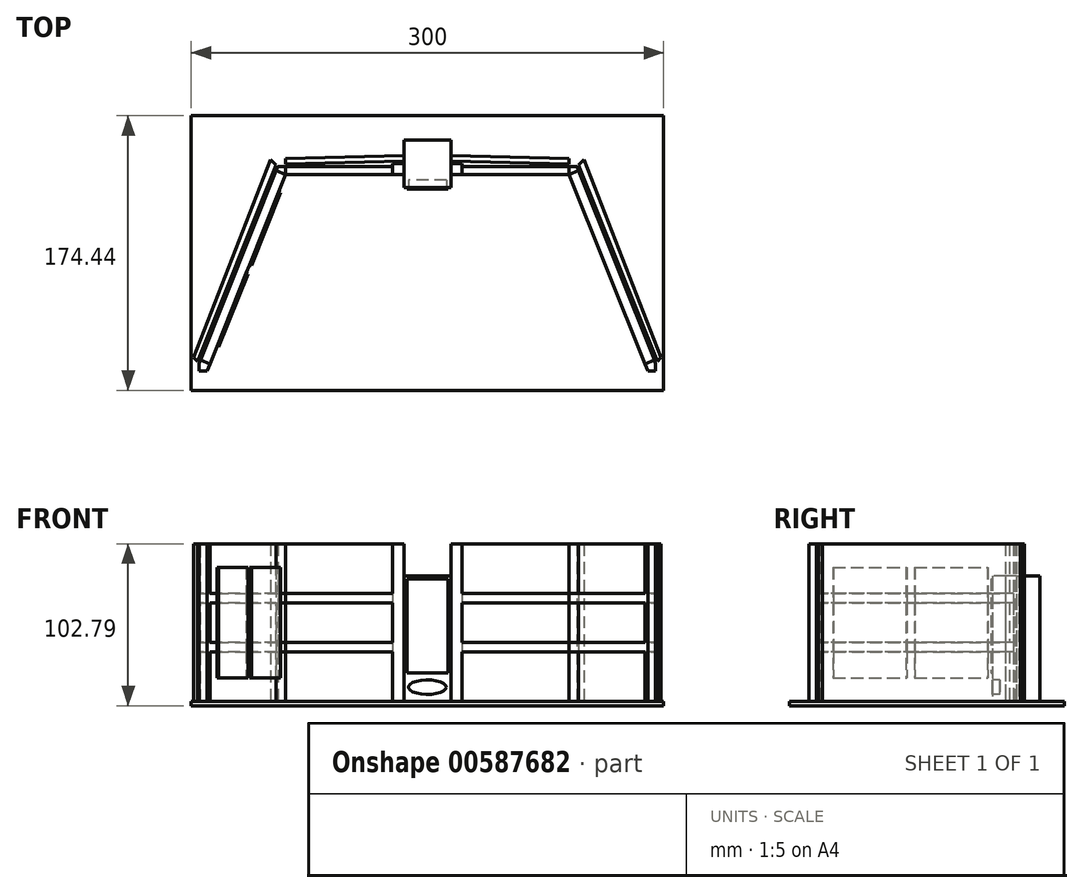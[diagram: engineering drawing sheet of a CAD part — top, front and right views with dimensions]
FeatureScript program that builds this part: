
annotation { "Feature Type Name" : "Feature", "Feature Type Description" : "" }
export const myFeature = defineFeature(function(context is Context, id is Id, definition is map)
    precondition{}
    {
        {
            var Q0;
            Q0=qCreatedBy(makeId("Top.planeOp"),FACE);
            var sketch = newSketch(context, id + "F0", { "sketchPlane" : qUnion([Q0])});
            skLineSegment(sketch, "E0.bottom", {"start": v(150, 87.22) * mm, "end": v(-150, 87.22) * mm});
            skLineSegment(sketch, "E0.top", {"start": v(150, -87.22) * mm, "end": v(-150, -87.22) * mm});
            skLineSegment(sketch, "E0.left", {"start": v(150, 87.22) * mm, "end": v(150, -87.22) * mm});
            skLineSegment(sketch, "E0.right", {"start": v(-150, 87.22) * mm, "end": v(-150, -87.22) * mm});
            skPoint(sketch, "E0.middle", {"position": v(0, 0) * mm});
            skSolve(sketch);
        }
        {
            var Q0;
            Q0 = qSketchRegion(id + "F0", true);
            extrude(context, id + "F1", {"entities" : qUnion([Q0]), "depth" : 2.8 * mm, "offsetDistance" : 25.4 * mm});
        }
        {
            var Q0;
            Q0=makeQuery(id+"F1.opExtrude","CAP_FACE",FACE,{"disambiguationData":[OSD([sQuery(id+"F0.wireOp",EDGE,"E0.bottom"),sQuery(id+"F0.wireOp",EDGE,"E0.top"),sQuery(id+"F0.wireOp",EDGE,"E0.left"),sQuery(id+"F0.wireOp",EDGE,"E0.right")])],"isStart":false});
            var sketch = newSketch(context, id + "F2", { "sketchPlane" : qUnion([Q0])});
            skLineSegment(sketch, "E1.bottom", {"start": v(-140, -70) * mm, "end": v(-145, -70) * mm});
            skLineSegment(sketch, "E1.top", {"start": v(-140, -75) * mm, "end": v(-145, -75) * mm});
            skLineSegment(sketch, "E1.left", {"start": v(-140, -70) * mm, "end": v(-140, -75) * mm});
            skLineSegment(sketch, "E1.right", {"start": v(-145, -70) * mm, "end": v(-145, -75) * mm});
            skPoint(sketch, "E1.middle", {"position": v(-142.5, -72.5) * mm});
            skLineSegment(sketch, "E2.bottom", {"start": v(-90, 50) * mm, "end": v(-95, 50) * mm});
            skLineSegment(sketch, "E2.top", {"start": v(-90, 55) * mm, "end": v(-95, 55) * mm});
            skLineSegment(sketch, "E2.left", {"start": v(-90, 50) * mm, "end": v(-90, 55) * mm});
            skLineSegment(sketch, "E2.right", {"start": v(-95, 50) * mm, "end": v(-95, 55) * mm});
            skPoint(sketch, "E2.middle", {"position": v(-92.5, 52.5) * mm});
            skLineSegment(sketch, "E3.bottom", {"start": v(95, 50) * mm, "end": v(90, 50) * mm});
            skLineSegment(sketch, "E3.top", {"start": v(95, 55) * mm, "end": v(90, 55) * mm});
            skLineSegment(sketch, "E3.left", {"start": v(95, 50) * mm, "end": v(95, 55) * mm});
            skLineSegment(sketch, "E3.right", {"start": v(90, 50) * mm, "end": v(90, 55) * mm});
            skPoint(sketch, "E3.middle", {"position": v(92.5, 52.5) * mm});
            skLineSegment(sketch, "E4.bottom", {"start": v(145, -75) * mm, "end": v(140, -75) * mm});
            skLineSegment(sketch, "E4.top", {"start": v(145, -70) * mm, "end": v(140, -70) * mm});
            skLineSegment(sketch, "E4.left", {"start": v(145, -75) * mm, "end": v(145, -70) * mm});
            skLineSegment(sketch, "E4.right", {"start": v(140, -75) * mm, "end": v(140, -70) * mm});
            skPoint(sketch, "E4.middle", {"position": v(142.5, -72.5) * mm});
            skLineSegment(sketch, "E5", {"start": v(0, 87.22) * mm, "end": v(0, -87.22) * mm, "construction": true});
            skLineSegment(sketch, "E6", {"start": v(-150, 0) * mm, "end": v(150, 0) * mm, "construction": true});
            skLineSegment(sketch, "E7.bottom", {"start": v(-15, 50) * mm, "end": v(-22, 50) * mm});
            skLineSegment(sketch, "E7.top", {"start": v(-15, 57) * mm, "end": v(-22, 57) * mm});
            skLineSegment(sketch, "E7.left", {"start": v(-15, 50) * mm, "end": v(-15, 57) * mm});
            skLineSegment(sketch, "E7.right", {"start": v(-22, 50) * mm, "end": v(-22, 57) * mm});
            skPoint(sketch, "E7.middle", {"position": v(-18.5, 53.5) * mm});
            skLineSegment(sketch, "E8.bottom", {"start": v(22, 50) * mm, "end": v(15, 50) * mm});
            skLineSegment(sketch, "E8.top", {"start": v(22, 57) * mm, "end": v(15, 57) * mm});
            skLineSegment(sketch, "E8.left", {"start": v(22, 50) * mm, "end": v(22, 57) * mm});
            skLineSegment(sketch, "E8.right", {"start": v(15, 50) * mm, "end": v(15, 57) * mm});
            skPoint(sketch, "E8.middle", {"position": v(18.5, 53.5) * mm});
            skPoint(sketch, "E9", {"position": v(-95, 52.5) * mm});
            skPoint(sketch, "E10", {"position": v(-15, 58.5) * mm});
            skPoint(sketch, "E11", {"position": v(-15, 62) * mm});
            skPoint(sketch, "E12", {"position": v(-90, 60) * mm});
            skPoint(sketch, "E13", {"position": v(-90, 56.5) * mm});
            skLineSegment(sketch, "E14", {"start": v(-90, 56.5) * mm, "end": v(-15, 58.5) * mm});
            skLineSegment(sketch, "E15", {"start": v(-15, 62) * mm, "end": v(-90, 60) * mm});
            skLineSegment(sketch, "E16", {"start": v(-90, 60) * mm, "end": v(-90, 56.5) * mm});
            skLineSegment(sketch, "E17", {"start": v(-15, 58.5) * mm, "end": v(-15, 62) * mm});
            skPoint(sketch, "E18", {"position": v(15, 58.5) * mm});
            skPoint(sketch, "E19", {"position": v(15, 62) * mm});
            skPoint(sketch, "E20", {"position": v(90, 56.5) * mm});
            skPoint(sketch, "E20.positionSnap0", {"position": v(90, 52.5) * mm});
            skPoint(sketch, "E21", {"position": v(90, 60) * mm});
            skLineSegment(sketch, "E22", {"start": v(15, 62) * mm, "end": v(90, 60) * mm});
            skLineSegment(sketch, "E23", {"start": v(90, 56.5) * mm, "end": v(90, 60) * mm});
            skLineSegment(sketch, "E24", {"start": v(90, 56.5) * mm, "end": v(15, 58.5) * mm});
            skLineSegment(sketch, "E25", {"start": v(15, 58.5) * mm, "end": v(15, 62) * mm});
            skLineSegment(sketch, "E26", {"start": v(95, 55) * mm, "end": v(100, 55) * mm, "construction": true});
            skLineSegment(sketch, "E27", {"start": v(95, 55) * mm, "end": v(95, 60) * mm, "construction": true});
            skLineSegment(sketch, "E28", {"start": v(95, 55) * mm, "end": v(102.6, 62.6) * mm, "construction": true});
            skPoint(sketch, "E29", {"position": v(96.06, 56.06) * mm});
            skPoint(sketch, "E30", {"position": v(99.56, 59.56) * mm});
            skPoint(sketch, "E31", {"position": v(145, -70) * mm});
            skLineSegment(sketch, "E32", {"start": v(140, -75) * mm, "end": v(149, -65.9) * mm, "construction": true});
            skPoint(sketch, "E33", {"position": v(146.03, -68.9) * mm});
            skPoint(sketch, "E34", {"position": v(148.5, -66.42) * mm});
            skLineSegment(sketch, "E35", {"start": v(146.03, -68.9) * mm, "end": v(96.06, 56.06) * mm});
            skLineSegment(sketch, "E36", {"start": v(96.06, 56.06) * mm, "end": v(99.56, 59.56) * mm});
            skLineSegment(sketch, "E37", {"start": v(99.56, 59.56) * mm, "end": v(148.5, -66.42) * mm});
            skLineSegment(sketch, "E38", {"start": v(146.03, -68.9) * mm, "end": v(148.5, -66.42) * mm});
            skLineSegment(sketch, "E39", {"start": v(-145, -70) * mm, "end": v(-145, -65) * mm, "construction": true});
            skLineSegment(sketch, "E40", {"start": v(-145, -70) * mm, "end": v(-150, -70) * mm, "construction": true});
            skPoint(sketch, "E41", {"position": v(-147.5, -70) * mm});
            skPoint(sketch, "E42", {"position": v(-145, -67.5) * mm});
            skLineSegment(sketch, "E43", {"start": v(-140, -75) * mm, "end": v(-149.1, -65.9) * mm, "construction": true});
            skPoint(sketch, "E44", {"position": v(-146.06, -68.94) * mm});
            skPoint(sketch, "E45", {"position": v(-148.54, -66.46) * mm});
            skLineSegment(sketch, "E46", {"start": v(-95, 55) * mm, "end": v(-95, 60) * mm, "construction": true});
            skLineSegment(sketch, "E47", {"start": v(-95, 60) * mm, "end": v(-95, 55) * mm, "construction": true});
            skLineSegment(sketch, "E48", {"start": v(-95, 55) * mm, "end": v(-100, 55) * mm, "construction": true});
            skPoint(sketch, "E49", {"position": v(-97.5, 55) * mm});
            skPoint(sketch, "E50", {"position": v(-95, 57.5) * mm});
            skLineSegment(sketch, "E51", {"start": v(-90, 50) * mm, "end": v(-100.8, 60.8) * mm, "construction": true});
            skPoint(sketch, "E52", {"position": v(-96.06, 56.06) * mm});
            skPoint(sketch, "E53", {"position": v(-99.56, 59.56) * mm});
            skLineSegment(sketch, "E54", {"start": v(-99.56, 59.56) * mm, "end": v(-148.54, -66.46) * mm});
            skLineSegment(sketch, "E55", {"start": v(-148.54, -66.46) * mm, "end": v(-146.06, -68.94) * mm});
            skLineSegment(sketch, "E56", {"start": v(-146.06, -68.94) * mm, "end": v(-96.06, 56.06) * mm});
            skLineSegment(sketch, "E57", {"start": v(-96.06, 56.06) * mm, "end": v(-99.56, 59.56) * mm});
            skSolve(sketch);
        }
        {
            var Q0;
            Q0 = qSketchRegion(id + "F2", true);
            extrude(context, id + "F3", {"entities" : qUnion([Q0]), "operationType" : NewBodyOperationType.ADD, "depth" : 100 * mm, "offsetDistance" : 25 * mm});
        }
        {
            var Q0;
            Q0=makeQuery(id+"F1.opExtrude","CAP_FACE",FACE,{"disambiguationData":[OSD([sQuery(id+"F0.wireOp",EDGE,"E0.bottom"),sQuery(id+"F0.wireOp",EDGE,"E0.top"),sQuery(id+"F0.wireOp",EDGE,"E0.left"),sQuery(id+"F0.wireOp",EDGE,"E0.right")])],"isStart":false});
            var sketch = newSketch(context, id + "F4", { "sketchPlane" : qUnion([Q0])});
            skLineSegment(sketch, "E58.bottom", {"start": v(-15, 71.7) * mm, "end": v(15, 71.7) * mm});
            skLineSegment(sketch, "E58.top", {"start": v(-15, 41.7) * mm, "end": v(15, 41.7) * mm});
            skLineSegment(sketch, "E58.left", {"start": v(-15, 71.7) * mm, "end": v(-15, 41.7) * mm});
            skLineSegment(sketch, "E58.right", {"start": v(15, 71.7) * mm, "end": v(15, 41.7) * mm});
            skLineSegment(sketch, "E59", {"start": v(-150, 50.01) * mm, "end": v(150, 50.01) * mm, "construction": true});
            skLineSegment(sketch, "E60", {"start": v(0, 87.22) * mm, "end": v(0, -87.22) * mm, "construction": true});
            skSolve(sketch);
        }
        {
            var Q0;
            Q0 = qSketchRegion(id + "F4", true);
            extrude(context, id + "F5", {"entities" : qUnion([Q0]), "operationType" : NewBodyOperationType.ADD, "depth" : 79.6 * mm, "offsetDistance" : 25 * mm});
        }
        {
            var Q0;
            Q0=makeQuery(id+"F5.opExtrude","SWEPT_FACE",FACE,{"disambiguationData":[OSD([sQuery(id+"F4.wireOp",EDGE,"E58.top")])]});
            var sketch = newSketch(context, id + "F6", { "sketchPlane" : qUnion([Q0])});
            skLineSegment(sketch, "E61.bottom", {"start": v(-13, 80.4) * mm, "end": v(13, 80.4) * mm});
            skLineSegment(sketch, "E61.top", {"start": v(-13, 20.8) * mm, "end": v(13, 20.8) * mm});
            skLineSegment(sketch, "E61.left", {"start": v(-13, 80.4) * mm, "end": v(-13, 20.8) * mm});
            skLineSegment(sketch, "E61.right", {"start": v(13, 80.4) * mm, "end": v(13, 20.8) * mm});
            skSolve(sketch);
        }
        {
            var Q0;
            Q0 = qSketchRegion(id + "F6", true);
            extrude(context, id + "F7", {"entities" : qUnion([Q0]), "operationType" : NewBodyOperationType.ADD, "depth" : 1.1 * mm, "offsetDistance" : 25 * mm});
        }
        {
            var Q0;
            Q0=makeQuery(id+"F5.opExtrude","SWEPT_FACE",FACE,{"disambiguationData":[OSD([sQuery(id+"F4.wireOp",EDGE,"E58.top")])]});
            var sketch = newSketch(context, id + "F8", { "sketchPlane" : qUnion([Q0])});
            skEllipse(sketch, "E62", {"center": v(0, 11.8) * mm, "majorRadius": 12.07 * mm, "minorRadius": 4.57 * mm, "majorAxis": v(1, 0)});
            skLineSegment(sketch, "E63", {"start": v(0, 2.8) * mm, "end": v(0, 20.8) * mm, "construction": true});
            skSolve(sketch);
        }
        {
            var Q0;
            Q0 = qSketchRegion(id + "F8", true);
            extrude(context, id + "F9", {"entities" : qUnion([Q0]), "operationType" : NewBodyOperationType.REMOVE, "oppositeDirection" : true, "depth" : 4.8 * mm, "offsetDistance" : 25 * mm});
        }
        {
            var Q0;
            Q0=makeQuery(id+"F1.opExtrude","CAP_FACE",FACE,{"disambiguationData":[OSD([sQuery(id+"F0.wireOp",EDGE,"E0.bottom"),sQuery(id+"F0.wireOp",EDGE,"E0.top"),sQuery(id+"F0.wireOp",EDGE,"E0.left"),sQuery(id+"F0.wireOp",EDGE,"E0.right")])],"isStart":false});
            var sketch = newSketch(context, id + "F10", { "sketchPlane" : qUnion([Q0])});
            skLineSegment(sketch, "E64", {"start": v(-140, -75) * mm, "end": v(-90, 50) * mm});
            skLineSegment(sketch, "E65", {"start": v(-145, -70) * mm, "end": v(-95, 55) * mm});
            skLineSegment(sketch, "E66", {"start": v(-90, 50) * mm, "end": v(-22, 50) * mm});
            skLineSegment(sketch, "E67", {"start": v(-90, 55) * mm, "end": v(-22, 55) * mm});
            skLineSegment(sketch, "E68", {"start": v(90, 55) * mm, "end": v(22, 55) * mm});
            skLineSegment(sketch, "E69", {"start": v(140, -75) * mm, "end": v(90, 50) * mm});
            skLineSegment(sketch, "E70", {"start": v(90, 50) * mm, "end": v(22, 50) * mm});
            skLineSegment(sketch, "E71", {"start": v(95, 55) * mm, "end": v(145, -70) * mm});
            skSolve(sketch);
        }
        {
            var Q0;
            Q0=makeQuery(id+"F10.imprint","IMPRINT",FACE,{"disambiguationData":[TD([[makeQuery(id+"F10.imprint","IMPRINT",EDGE,{"derivedFrom":sQuery(id+"F10.wireOp",EDGE,"E64")}),1.0]])]});
            extrude(context, id + "F11", {"entities" : qUnion([Q0]), "operationType" : NewBodyOperationType.ADD, "depth" : 100 * mm, "offsetDistance" : 25 * mm});
        }
        {
            var Q0;
            Q0=makeQuery(id+"F1.opExtrude","CAP_FACE",FACE,{"disambiguationData":[OSD([sQuery(id+"F0.wireOp",EDGE,"E0.bottom"),sQuery(id+"F0.wireOp",EDGE,"E0.top"),sQuery(id+"F0.wireOp",EDGE,"E0.left"),sQuery(id+"F0.wireOp",EDGE,"E0.right")])],"isStart":false});
            var sketch = newSketch(context, id + "F12", { "sketchPlane" : qUnion([Q0])});
            skLineSegment(sketch, "E72", {"start": v(-90, 50) * mm, "end": v(-22, 50) * mm});
            skLineSegment(sketch, "E73", {"start": v(-90, 55) * mm, "end": v(-22, 55) * mm});
            skSolve(sketch);
        }
        {
            var Q0;
            Q0 = qSketchRegion(id + "F12", true);
            var Q1;
            {var subQ0=sQuery(id+"F12.wireOp",EDGE,"E72");Q1=makeQuery(id+"F12.imprint","IMPRINT",FACE,{"disambiguationData":[TD([[makeQuery(id+"F12.imprint","IMPRINT",EDGE,{"derivedFrom":subQ0}),1.0]])]});}
            extrude(context, id + "F13", {"entities" : qUnion([Q0, Q1]), "operationType" : NewBodyOperationType.ADD, "depth" : 100 * mm, "offsetDistance" : 25 * mm});
        }
        {
            var Q0;
            Q0=makeQuery(id+"F1.opExtrude","CAP_FACE",FACE,{"disambiguationData":[OSD([sQuery(id+"F0.wireOp",EDGE,"E0.bottom"),sQuery(id+"F0.wireOp",EDGE,"E0.top"),sQuery(id+"F0.wireOp",EDGE,"E0.left"),sQuery(id+"F0.wireOp",EDGE,"E0.right")])],"isStart":false});
            var sketch = newSketch(context, id + "F14", { "sketchPlane" : qUnion([Q0])});
            skLineSegment(sketch, "E74", {"start": v(22, 50) * mm, "end": v(90, 50) * mm});
            skLineSegment(sketch, "E75", {"start": v(90, 55) * mm, "end": v(22, 55) * mm});
            skSolve(sketch);
        }
        {
            var Q0;
            Q0 = qSketchRegion(id + "F14", true);
            var Q1;
            {var subQ0=sQuery(id+"F14.wireOp",EDGE,"E74");Q1=makeQuery(id+"F14.imprint","IMPRINT",FACE,{"disambiguationData":[TD([[makeQuery(id+"F14.imprint","IMPRINT",EDGE,{"derivedFrom":subQ0}),1.0]])]});}
            extrude(context, id + "F15", {"entities" : qUnion([Q0, Q1]), "operationType" : NewBodyOperationType.ADD, "depth" : 100 * mm, "offsetDistance" : 25 * mm});
        }
        {
            var Q0;
            Q0=makeQuery(id+"F1.opExtrude","CAP_FACE",FACE,{"disambiguationData":[OSD([sQuery(id+"F0.wireOp",EDGE,"E0.bottom"),sQuery(id+"F0.wireOp",EDGE,"E0.top"),sQuery(id+"F0.wireOp",EDGE,"E0.left"),sQuery(id+"F0.wireOp",EDGE,"E0.right")])],"isStart":false});
            var sketch = newSketch(context, id + "F16", { "sketchPlane" : qUnion([Q0])});
            skLineSegment(sketch, "E76", {"start": v(140, -75) * mm, "end": v(90, 50) * mm});
            skLineSegment(sketch, "E77", {"start": v(145, -70) * mm, "end": v(95, 55) * mm});
            skSolve(sketch);
        }
        {
            var Q0;
            Q0 = qSketchRegion(id + "F16", true);
            var Q1;
            Q1=makeQuery(id+"F16.imprint","IMPRINT",FACE,{"disambiguationData":[TD([[makeQuery(id+"F16.imprint","IMPRINT",EDGE,{"derivedFrom":sQuery(id+"F16.wireOp",EDGE,"E76")}),-1.0]])]});
            extrude(context, id + "F17", {"entities" : qUnion([Q0, Q1]), "operationType" : NewBodyOperationType.ADD, "depth" : 100 * mm, "offsetDistance" : 25 * mm});
        }
        {
            var Q0;
            Q0=makeQuery(id+"F11.opExtrude","SWEPT_FACE",FACE,{"disambiguationData":[OSD([sQuery(id+"F10.wireOp",EDGE,"E64")])]});
            var sketch = newSketch(context, id + "F18", { "sketchPlane" : qUnion([Q0])});
            skLineSegment(sketch, "E78.bottom", {"start": v(-116.63, 102.8) * mm, "end": v(13, 102.8) * mm});
            skLineSegment(sketch, "E78.top", {"start": v(-116.63, 71.3) * mm, "end": v(13, 71.3) * mm});
            skLineSegment(sketch, "E78.left", {"start": v(-116.63, 102.8) * mm, "end": v(-116.63, 71.3) * mm});
            skLineSegment(sketch, "E78.right", {"start": v(13, 102.8) * mm, "end": v(13, 71.3) * mm});
            skLineSegment(sketch, "E79.bottom", {"start": v(-116.63, 65.3) * mm, "end": v(13, 65.3) * mm});
            skLineSegment(sketch, "E79.top", {"start": v(-116.63, 40.3) * mm, "end": v(13, 40.3) * mm});
            skLineSegment(sketch, "E79.left", {"start": v(-116.63, 65.3) * mm, "end": v(-116.63, 40.3) * mm});
            skLineSegment(sketch, "E79.right", {"start": v(13, 65.3) * mm, "end": v(13, 40.3) * mm});
            skLineSegment(sketch, "E80.bottom", {"start": v(-116.63, 34.3) * mm, "end": v(13, 34.3) * mm});
            skLineSegment(sketch, "E80.top", {"start": v(-116.63, 2.8) * mm, "end": v(13, 2.8) * mm});
            skLineSegment(sketch, "E80.left", {"start": v(-116.63, 34.3) * mm, "end": v(-116.63, 2.8) * mm});
            skLineSegment(sketch, "E80.right", {"start": v(13, 34.3) * mm, "end": v(13, 2.8) * mm});
            skSolve(sketch);
        }
        {
            var Q0;
            Q0=makeQuery(id+"F18.imprint","IMPRINT",FACE,{"disambiguationData":[TD([[makeQuery(id+"F18.imprint","IMPRINT",EDGE,{"derivedFrom":sQuery(id+"F18.wireOp",EDGE,"E78.bottom")}),-1.0]])]});
            var Q1;
            Q1=makeQuery(id+"F18.imprint","IMPRINT",FACE,{"disambiguationData":[TD([[makeQuery(id+"F18.imprint","IMPRINT",EDGE,{"derivedFrom":sQuery(id+"F18.wireOp",EDGE,"E79.bottom")}),-1.0]])]});
            var Q2;
            Q2=makeQuery(id+"F18.imprint","IMPRINT",FACE,{"disambiguationData":[TD([[makeQuery(id+"F18.imprint","IMPRINT",EDGE,{"derivedFrom":sQuery(id+"F18.wireOp",EDGE,"E80.bottom")}),-1.0]])]});
            extrude(context, id + "F19", {"entities" : qUnion([Q0, Q1, Q2]), "operationType" : NewBodyOperationType.REMOVE, "oppositeDirection" : true, "depth" : 16.5 * mm, "offsetDistance" : 25 * mm});
        }
        {
            var Q0;
            Q0=makeQuery(id+"F13.boolean.opBoolean","MERGE",FACE,{"derivedFrom":[makeQuery(id+"F3.opExtrude","SWEPT_FACE",FACE,{"disambiguationData":[OSD([sQuery(id+"F2.wireOp",EDGE,"E7.bottom")])]}),makeQuery(id+"F13.opExtrude","SWEPT_FACE",FACE,{"disambiguationData":[OSD([sQuery(id+"F12.wireOp",EDGE,"E72")])]})]});
            var sketch = newSketch(context, id + "F20", { "sketchPlane" : qUnion([Q0])});
            skLineSegment(sketch, "E81.bottom", {"start": v(-90, 34.3) * mm, "end": v(-22, 34.3) * mm});
            skLineSegment(sketch, "E81.top", {"start": v(-90, 2.8) * mm, "end": v(-22, 2.8) * mm});
            skLineSegment(sketch, "E81.left", {"start": v(-90, 34.3) * mm, "end": v(-90, 2.8) * mm});
            skLineSegment(sketch, "E81.right", {"start": v(-22, 34.3) * mm, "end": v(-22, 2.8) * mm});
            skLineSegment(sketch, "E82.bottom", {"start": v(-90, 102.8) * mm, "end": v(-22, 102.8) * mm});
            skLineSegment(sketch, "E82.top", {"start": v(-90, 71.3) * mm, "end": v(-22, 71.3) * mm});
            skLineSegment(sketch, "E82.left", {"start": v(-90, 102.8) * mm, "end": v(-90, 71.3) * mm});
            skLineSegment(sketch, "E82.right", {"start": v(-22, 102.8) * mm, "end": v(-22, 71.3) * mm});
            skLineSegment(sketch, "E83.bottom", {"start": v(-90, 65.3) * mm, "end": v(-22, 65.3) * mm});
            skLineSegment(sketch, "E83.top", {"start": v(-90, 40.3) * mm, "end": v(-22, 40.3) * mm});
            skLineSegment(sketch, "E83.left", {"start": v(-90, 65.3) * mm, "end": v(-90, 40.3) * mm});
            skLineSegment(sketch, "E83.right", {"start": v(-22, 65.3) * mm, "end": v(-22, 40.3) * mm});
            skSolve(sketch);
        }
        {
            var Q0;
            Q0=makeQuery(id+"F20.imprint","IMPRINT",FACE,{"disambiguationData":[TD([[makeQuery(id+"F20.imprint","IMPRINT",EDGE,{"derivedFrom":sQuery(id+"F20.wireOp",EDGE,"E82.bottom")}),1.0]])]});
            var Q1;
            Q1=makeQuery(id+"F20.imprint","IMPRINT",FACE,{"disambiguationData":[TD([[makeQuery(id+"F20.imprint","IMPRINT",EDGE,{"derivedFrom":sQuery(id+"F20.wireOp",EDGE,"E83.bottom")}),-1.0]])]});
            var Q2;
            Q2=makeQuery(id+"F20.imprint","IMPRINT",FACE,{"disambiguationData":[TD([[makeQuery(id+"F20.imprint","IMPRINT",EDGE,{"derivedFrom":sQuery(id+"F20.wireOp",EDGE,"E81.bottom")}),-1.0]])]});
            extrude(context, id + "F21", {"entities" : qUnion([Q0, Q1, Q2]), "operationType" : NewBodyOperationType.REMOVE, "oppositeDirection" : true, "depth" : 25 * mm, "offsetDistance" : 25 * mm});
        }
        {
            var Q0;
            Q0=makeQuery(id+"F15.boolean.opBoolean","MERGE",FACE,{"derivedFrom":[makeQuery(id+"F3.opExtrude","SWEPT_FACE",FACE,{"disambiguationData":[OSD([sQuery(id+"F2.wireOp",EDGE,"E3.bottom")])]}),makeQuery(id+"F3.opExtrude","SWEPT_FACE",FACE,{"disambiguationData":[OSD([sQuery(id+"F2.wireOp",EDGE,"E8.bottom")])]}),makeQuery(id+"F15.opExtrude","SWEPT_FACE",FACE,{"disambiguationData":[OSD([sQuery(id+"F14.wireOp",EDGE,"E74")])]})]});
            var sketch = newSketch(context, id + "F22", { "sketchPlane" : qUnion([Q0])});
            skLineSegment(sketch, "E84.bottom", {"start": v(90, 102.8) * mm, "end": v(22, 102.8) * mm});
            skLineSegment(sketch, "E84.top", {"start": v(90, 71.3) * mm, "end": v(22, 71.3) * mm});
            skLineSegment(sketch, "E84.left", {"start": v(90, 102.8) * mm, "end": v(90, 71.3) * mm});
            skLineSegment(sketch, "E84.right", {"start": v(22, 102.8) * mm, "end": v(22, 71.3) * mm});
            skLineSegment(sketch, "E85.bottom", {"start": v(90, 65.3) * mm, "end": v(22, 65.3) * mm});
            skLineSegment(sketch, "E85.top", {"start": v(90, 40.3) * mm, "end": v(22, 40.3) * mm});
            skLineSegment(sketch, "E85.left", {"start": v(90, 65.3) * mm, "end": v(90, 40.3) * mm});
            skLineSegment(sketch, "E85.right", {"start": v(22, 65.3) * mm, "end": v(22, 40.3) * mm});
            skLineSegment(sketch, "E86.bottom", {"start": v(90, 34.3) * mm, "end": v(22, 34.3) * mm});
            skLineSegment(sketch, "E86.top", {"start": v(90, 2.8) * mm, "end": v(22, 2.8) * mm});
            skLineSegment(sketch, "E86.left", {"start": v(90, 34.3) * mm, "end": v(90, 2.8) * mm});
            skLineSegment(sketch, "E86.right", {"start": v(22, 34.3) * mm, "end": v(22, 2.8) * mm});
            skSolve(sketch);
        }
        {
            var Q0;
            Q0=makeQuery(id+"F22.imprint","IMPRINT",FACE,{"disambiguationData":[TD([[makeQuery(id+"F22.imprint","IMPRINT",EDGE,{"derivedFrom":sQuery(id+"F22.wireOp",EDGE,"E86.bottom")}),1.0]])]});
            var Q1;
            Q1=makeQuery(id+"F22.imprint","IMPRINT",FACE,{"disambiguationData":[TD([[makeQuery(id+"F22.imprint","IMPRINT",EDGE,{"derivedFrom":sQuery(id+"F22.wireOp",EDGE,"E85.bottom")}),1.0]])]});
            var Q2;
            Q2=makeQuery(id+"F22.imprint","IMPRINT",FACE,{"disambiguationData":[TD([[makeQuery(id+"F22.imprint","IMPRINT",EDGE,{"derivedFrom":sQuery(id+"F22.wireOp",EDGE,"E84.bottom")}),1.0]])]});
            extrude(context, id + "F23", {"entities" : qUnion([Q0, Q1, Q2]), "operationType" : NewBodyOperationType.REMOVE, "oppositeDirection" : true, "depth" : 25 * mm, "offsetDistance" : 25 * mm});
        }
        {
            var Q0;
            Q0=makeQuery(id+"F17.opExtrude","SWEPT_FACE",FACE,{"disambiguationData":[OSD([sQuery(id+"F16.wireOp",EDGE,"E76")])]});
            var sketch = newSketch(context, id + "F24", { "sketchPlane" : qUnion([Q0])});
            skLineSegment(sketch, "E87.bottom", {"start": v(-13, 102.8) * mm, "end": v(116.63, 102.8) * mm});
            skLineSegment(sketch, "E87.top", {"start": v(-13, 71.3) * mm, "end": v(116.63, 71.3) * mm});
            skLineSegment(sketch, "E87.left", {"start": v(-13, 102.8) * mm, "end": v(-13, 71.3) * mm});
            skLineSegment(sketch, "E87.right", {"start": v(116.63, 102.8) * mm, "end": v(116.63, 71.3) * mm});
            skLineSegment(sketch, "E88.bottom", {"start": v(-13, 65.3) * mm, "end": v(116.63, 65.3) * mm});
            skLineSegment(sketch, "E88.top", {"start": v(-13, 40.3) * mm, "end": v(116.63, 40.3) * mm});
            skLineSegment(sketch, "E88.left", {"start": v(-13, 65.3) * mm, "end": v(-13, 40.3) * mm});
            skLineSegment(sketch, "E88.right", {"start": v(116.63, 65.3) * mm, "end": v(116.63, 40.3) * mm});
            skLineSegment(sketch, "E89.bottom", {"start": v(-13, 34.3) * mm, "end": v(116.63, 34.3) * mm});
            skLineSegment(sketch, "E89.top", {"start": v(-13, 2.8) * mm, "end": v(116.63, 2.8) * mm});
            skLineSegment(sketch, "E89.left", {"start": v(-13, 34.3) * mm, "end": v(-13, 2.8) * mm});
            skLineSegment(sketch, "E89.right", {"start": v(116.63, 34.3) * mm, "end": v(116.63, 2.8) * mm});
            skSolve(sketch);
        }
        {
            var Q0;
            Q0=makeQuery(id+"F24.imprint","IMPRINT",FACE,{"disambiguationData":[TD([[makeQuery(id+"F24.imprint","IMPRINT",EDGE,{"derivedFrom":sQuery(id+"F24.wireOp",EDGE,"E87.bottom")}),1.0]])]});
            var Q1;
            Q1=makeQuery(id+"F24.imprint","IMPRINT",FACE,{"disambiguationData":[TD([[makeQuery(id+"F24.imprint","IMPRINT",EDGE,{"derivedFrom":sQuery(id+"F24.wireOp",EDGE,"E88.bottom")}),-1.0]])]});
            var Q2;
            Q2=makeQuery(id+"F24.imprint","IMPRINT",FACE,{"disambiguationData":[TD([[makeQuery(id+"F24.imprint","IMPRINT",EDGE,{"derivedFrom":sQuery(id+"F24.wireOp",EDGE,"E89.bottom")}),-1.0]])]});
            extrude(context, id + "F25", {"entities" : qUnion([Q0, Q1, Q2]), "operationType" : NewBodyOperationType.REMOVE, "oppositeDirection" : true, "depth" : 25 * mm, "offsetDistance" : 25 * mm});
        }
        {
            var Q0;
            Q0=makeQuery(id+"F2.imprint","IMPRINT",FACE,{"disambiguationData":[TD([[makeQuery(id+"F2.imprint","IMPRINT",EDGE,{"derivedFrom":sQuery(id+"F2.wireOp",EDGE,"E54")}),1.0]])]});
            var Q1;
            Q1=makeQuery(id+"F2.imprint","IMPRINT",FACE,{"disambiguationData":[TD([[makeQuery(id+"F2.imprint","IMPRINT",EDGE,{"derivedFrom":sQuery(id+"F2.wireOp",EDGE,"E14")}),1.0]])]});
            var Q2;
            Q2=makeQuery(id+"F2.imprint","IMPRINT",FACE,{"disambiguationData":[TD([[makeQuery(id+"F2.imprint","IMPRINT",EDGE,{"derivedFrom":sQuery(id+"F2.wireOp",EDGE,"E22")}),-1.0]])]});
            var Q3;
            Q3=makeQuery(id+"F2.imprint","IMPRINT",FACE,{"disambiguationData":[TD([[makeQuery(id+"F2.imprint","IMPRINT",EDGE,{"derivedFrom":sQuery(id+"F2.wireOp",EDGE,"E35")}),-1.0]])]});
            extrude(context, id + "F26", {"entities" : qUnion([Q0, Q1, Q2, Q3]), "operationType" : NewBodyOperationType.ADD, "depth" : 100 * mm, "offsetDistance" : 25 * mm});
        }
        {
            var Q0;
            Q0=makeQuery(id+"F11.opExtrude","SWEPT_FACE",FACE,{"disambiguationData":[OSD([sQuery(id+"F10.wireOp",EDGE,"E64")])]});
            var sketch = newSketch(context, id + "F27", { "sketchPlane" : qUnion([Q0])});
            skLineSegment(sketch, "E90.bottom", {"start": v(-104.63, 87.8) * mm, "end": v(-54.63, 87.8) * mm});
            skLineSegment(sketch, "E90.top", {"start": v(-104.63, 17.8) * mm, "end": v(-54.63, 17.8) * mm});
            skLineSegment(sketch, "E90.left", {"start": v(-104.63, 87.8) * mm, "end": v(-104.63, 17.8) * mm});
            skLineSegment(sketch, "E90.right", {"start": v(-54.63, 87.8) * mm, "end": v(-54.63, 17.8) * mm});
            skLineSegment(sketch, "E91.bottom", {"start": v(-49, 87.8) * mm, "end": v(1, 87.8) * mm});
            skLineSegment(sketch, "E91.top", {"start": v(-49, 17.8) * mm, "end": v(1, 17.8) * mm});
            skLineSegment(sketch, "E91.left", {"start": v(-49, 87.8) * mm, "end": v(-49, 17.8) * mm});
            skLineSegment(sketch, "E91.right", {"start": v(1, 87.8) * mm, "end": v(1, 17.8) * mm});
            skSolve(sketch);
        }
        {
            var Q0;
            {var subQ0=sQuery(id+"F27.wireOp",EDGE,"E90.bottom");Q0=makeQuery(id+"F27.imprint","IMPRINT",FACE,{"disambiguationData":[TD([[makeQuery(id+"F27.imprint","IMPRINT",EDGE,{"derivedFrom":subQ0}),-1.0]])]});}
            var Q1;
            {var subQ0=sQuery(id+"F27.wireOp",EDGE,"E90.left");var subQ1=makeQuery(id+"F19.boolean.opBoolean","COPY",EDGE,{"derivedFrom":makeQuery(id+"F19.opExtrude","CAP_EDGE",EDGE,{"disambiguationData":[OSD([sQuery(id+"F18.wireOp",EDGE,"E79.bottom")])],"isStart":true})});var subQ2=makeQuery(id+"F27.imprint","INTERSECT",VERTEX,{"derivedFrom":[subQ1,subQ0]});Q1=makeQuery(id+"F27.imprint","IMPRINT",FACE,{"disambiguationData":[TD([[makeQuery(id+"F27.imprint","IMPRINT",EDGE,{"disambiguationData":[TD([[subQ2,-1.0]])],"derivedFrom":subQ0}),1.0]])]});}
            var Q2;
            {var subQ0=sQuery(id+"F27.wireOp",EDGE,"E90.left");var subQ1=makeQuery(id+"F19.boolean.opBoolean","COPY",EDGE,{"derivedFrom":makeQuery(id+"F19.opExtrude","CAP_EDGE",EDGE,{"disambiguationData":[OSD([sQuery(id+"F18.wireOp",EDGE,"E78.top")])],"isStart":true})});var subQ2=makeQuery(id+"F27.imprint","INTERSECT",VERTEX,{"derivedFrom":[subQ1,subQ0]});Q2=makeQuery(id+"F27.imprint","IMPRINT",FACE,{"disambiguationData":[TD([[makeQuery(id+"F27.imprint","IMPRINT",EDGE,{"disambiguationData":[TD([[subQ2,-1.0]])],"derivedFrom":subQ0}),1.0]])]});}
            var Q3;
            {var subQ0=sQuery(id+"F27.wireOp",EDGE,"E90.top");Q3=makeQuery(id+"F27.imprint","IMPRINT",FACE,{"disambiguationData":[TD([[makeQuery(id+"F27.imprint","IMPRINT",EDGE,{"derivedFrom":subQ0}),1.0]])]});}
            var Q4;
            {var subQ0=sQuery(id+"F27.wireOp",EDGE,"E90.left");var subQ1=makeQuery(id+"F19.boolean.opBoolean","COPY",EDGE,{"derivedFrom":makeQuery(id+"F19.opExtrude","CAP_EDGE",EDGE,{"disambiguationData":[OSD([sQuery(id+"F18.wireOp",EDGE,"E80.bottom")])],"isStart":true})});var subQ2=makeQuery(id+"F27.imprint","INTERSECT",VERTEX,{"derivedFrom":[subQ1,subQ0]});Q4=makeQuery(id+"F27.imprint","IMPRINT",FACE,{"disambiguationData":[TD([[makeQuery(id+"F27.imprint","IMPRINT",EDGE,{"disambiguationData":[TD([[subQ2,1.0]])],"derivedFrom":subQ0}),1.0]])]});}
            var Q5;
            {var subQ0=sQuery(id+"F27.wireOp",EDGE,"E91.top");Q5=makeQuery(id+"F27.imprint","IMPRINT",FACE,{"disambiguationData":[TD([[makeQuery(id+"F27.imprint","IMPRINT",EDGE,{"derivedFrom":subQ0}),1.0]])]});}
            var Q6;
            {var subQ0=sQuery(id+"F27.wireOp",EDGE,"E91.left");var subQ1=makeQuery(id+"F19.boolean.opBoolean","COPY",EDGE,{"derivedFrom":makeQuery(id+"F19.opExtrude","CAP_EDGE",EDGE,{"disambiguationData":[OSD([sQuery(id+"F18.wireOp",EDGE,"E80.bottom")])],"isStart":true})});var subQ2=makeQuery(id+"F27.imprint","INTERSECT",VERTEX,{"derivedFrom":[subQ1,subQ0]});Q6=makeQuery(id+"F27.imprint","IMPRINT",FACE,{"disambiguationData":[TD([[makeQuery(id+"F27.imprint","IMPRINT",EDGE,{"disambiguationData":[TD([[subQ2,1.0]])],"derivedFrom":subQ0}),1.0]])]});}
            var Q7;
            {var subQ0=sQuery(id+"F27.wireOp",EDGE,"E91.left");var subQ1=makeQuery(id+"F19.boolean.opBoolean","COPY",EDGE,{"derivedFrom":makeQuery(id+"F19.opExtrude","CAP_EDGE",EDGE,{"disambiguationData":[OSD([sQuery(id+"F18.wireOp",EDGE,"E79.bottom")])],"isStart":true})});var subQ2=makeQuery(id+"F27.imprint","INTERSECT",VERTEX,{"derivedFrom":[subQ1,subQ0]});Q7=makeQuery(id+"F27.imprint","IMPRINT",FACE,{"disambiguationData":[TD([[makeQuery(id+"F27.imprint","IMPRINT",EDGE,{"disambiguationData":[TD([[subQ2,-1.0]])],"derivedFrom":subQ0}),1.0]])]});}
            var Q8;
            {var subQ0=sQuery(id+"F27.wireOp",EDGE,"E91.left");var subQ1=makeQuery(id+"F19.boolean.opBoolean","COPY",EDGE,{"derivedFrom":makeQuery(id+"F19.opExtrude","CAP_EDGE",EDGE,{"disambiguationData":[OSD([sQuery(id+"F18.wireOp",EDGE,"E78.top")])],"isStart":true})});var subQ2=makeQuery(id+"F27.imprint","INTERSECT",VERTEX,{"derivedFrom":[subQ1,subQ0]});Q8=makeQuery(id+"F27.imprint","IMPRINT",FACE,{"disambiguationData":[TD([[makeQuery(id+"F27.imprint","IMPRINT",EDGE,{"disambiguationData":[TD([[subQ2,-1.0]])],"derivedFrom":subQ0}),1.0]])]});}
            var Q9;
            {var subQ0=sQuery(id+"F27.wireOp",EDGE,"E91.bottom");Q9=makeQuery(id+"F27.imprint","IMPRINT",FACE,{"disambiguationData":[TD([[makeQuery(id+"F27.imprint","IMPRINT",EDGE,{"derivedFrom":subQ0}),-1.0]])]});}
            extrude(context, id + "F28", {"entities" : qUnion([Q0, Q1, Q2, Q3, Q4, Q5, Q6, Q7, Q8, Q9]), "operationType" : NewBodyOperationType.ADD, "depth" : 1.3 * mm, "offsetDistance" : 25 * mm});
        }
    });
